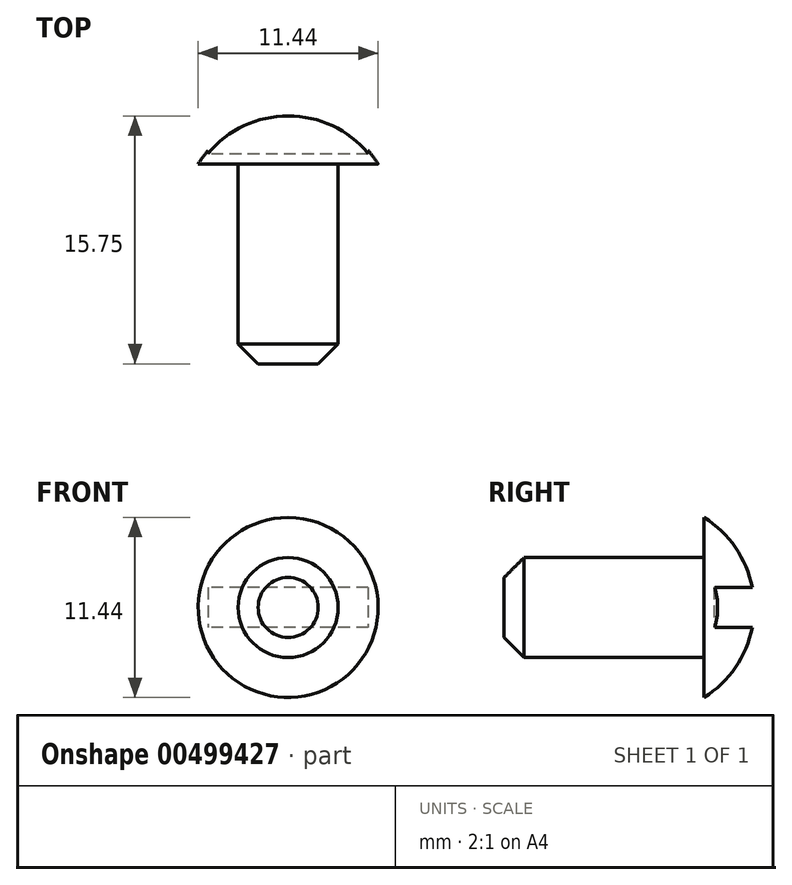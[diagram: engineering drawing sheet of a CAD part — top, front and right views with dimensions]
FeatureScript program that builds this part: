
annotation { "Feature Type Name" : "Feature", "Feature Type Description" : "" }
export const myFeature = defineFeature(function(context is Context, id is Id, definition is map)
    precondition{}
    {
        {
            var Q0;
            Q0=qCreatedBy(makeId("Top.planeOp"),FACE);
            var sketch = newSketch(context, id + "F0", { "sketchPlane" : qUnion([Q0])});
            skLineSegment(sketch, "E0", {"start": v(0, 83.21) * mm, "end": v(0, 0) * mm, "construction": true});
            skLineSegment(sketch, "E1", {"start": v(0, 0) * mm, "end": v(3.18, 0) * mm});
            skLineSegment(sketch, "E2", {"start": v(0, 12.7) * mm, "end": v(5.71, 12.7) * mm});
            skPoint(sketch, "E3", {"position": v(0, 15.88) * mm});
            skLineSegment(sketch, "E4", {"start": v(0, 15.88) * mm, "end": v(0, 0) * mm});
            skLineSegment(sketch, "E5", {"start": v(3.18, 0) * mm, "end": v(3.18, 12.7) * mm});
            skArc(sketch, "E6", {"start": v(5.71, 12.7) * mm, "mid": v(3.27, 15.03) * mm, "end": v(0, 15.88) * mm});
            skSolve(sketch);
        }
        {
            var Q0;
            {var subQ0=sQuery(id+"F0.wireOp",EDGE,"E1");Q0=makeQuery(id+"F0.imprint","IMPRINT",FACE,{"disambiguationData":[TD([[makeQuery(id+"F0.imprint","IMPRINT",EDGE,{"derivedFrom":subQ0}),1.0]])]});}
            var Q1;
            {var subQ4=sQuery(id+"F0.wireOp",EDGE,"E6");Q1=makeQuery(id+"F0.imprint","IMPRINT",FACE,{"disambiguationData":[TD([[makeQuery(id+"F0.imprint","IMPRINT",EDGE,{"derivedFrom":subQ4}),1.0]])]});}
            var Q2;
            Q2=sQuery(id+"F0.wireOp",EDGE,"E0");
            revolve(context, id + "F1", {"entities" : qUnion([Q0, Q1]), "axis" : qUnion([Q2]), "revolveType" : RevolveType.FULL});
        }
        {
            var Q0;
            Q0=makeQuery(id+"F1.opRevolve","SWEPT_FACE",FACE,{"disambiguationData":[OSD([sQuery(id+"F0.wireOp",EDGE,"E2")])]});
            cPlane(context, id + "F2", {"entities" : qUnion([Q0]), "cplaneType" : CPlaneType.OFFSET, "offset" : 0.64 * mm, "oppositeDirection" : true, "width" : 152.4 * mm, "height" : 152.4 * mm});
        }
        {
            var Q0;
            Q0=qCreatedBy(id+"F2.planeOp",FACE);
            var sketch = newSketch(context, id + "F3", { "sketchPlane" : qUnion([Q0])});
            skLineSegment(sketch, "E7.bottom", {"start": v(5.08, 1.27) * mm, "end": v(-5.08, 1.27) * mm});
            skLineSegment(sketch, "E7.top", {"start": v(5.08, -1.27) * mm, "end": v(-5.08, -1.27) * mm});
            skLineSegment(sketch, "E7.left", {"start": v(5.08, 1.27) * mm, "end": v(5.08, -1.27) * mm});
            skLineSegment(sketch, "E7.right", {"start": v(-5.08, 1.27) * mm, "end": v(-5.08, -1.27) * mm});
            skPoint(sketch, "E7.middle", {"position": v(0, 0) * mm});
            skSolve(sketch);
        }
        {
            var Q0;
            Q0 = qSketchRegion(id + "F3", true);
            extrude(context, id + "F4", {"entities" : qUnion([Q0]), "operationType" : NewBodyOperationType.REMOVE, "endBound" : BoundingType.THROUGH_ALL, "oppositeDirection" : true, "depth" : 25.4 * mm});
        }
        {
            var Q0;
            Q0=makeQuery(id+"F1.opRevolve","SWEPT_EDGE",EDGE,{"disambiguationData":[OSD([sQuery(id+"F0.wireOp",EDGE,"E1"),sQuery(id+"F0.wireOp",EDGE,"E5")])]});
            chamfer(context, id + "F5", {"entities" : qUnion([Q0]), "width" : 1.27 * mm, "tangentPropagation" : true});
        }
    });
